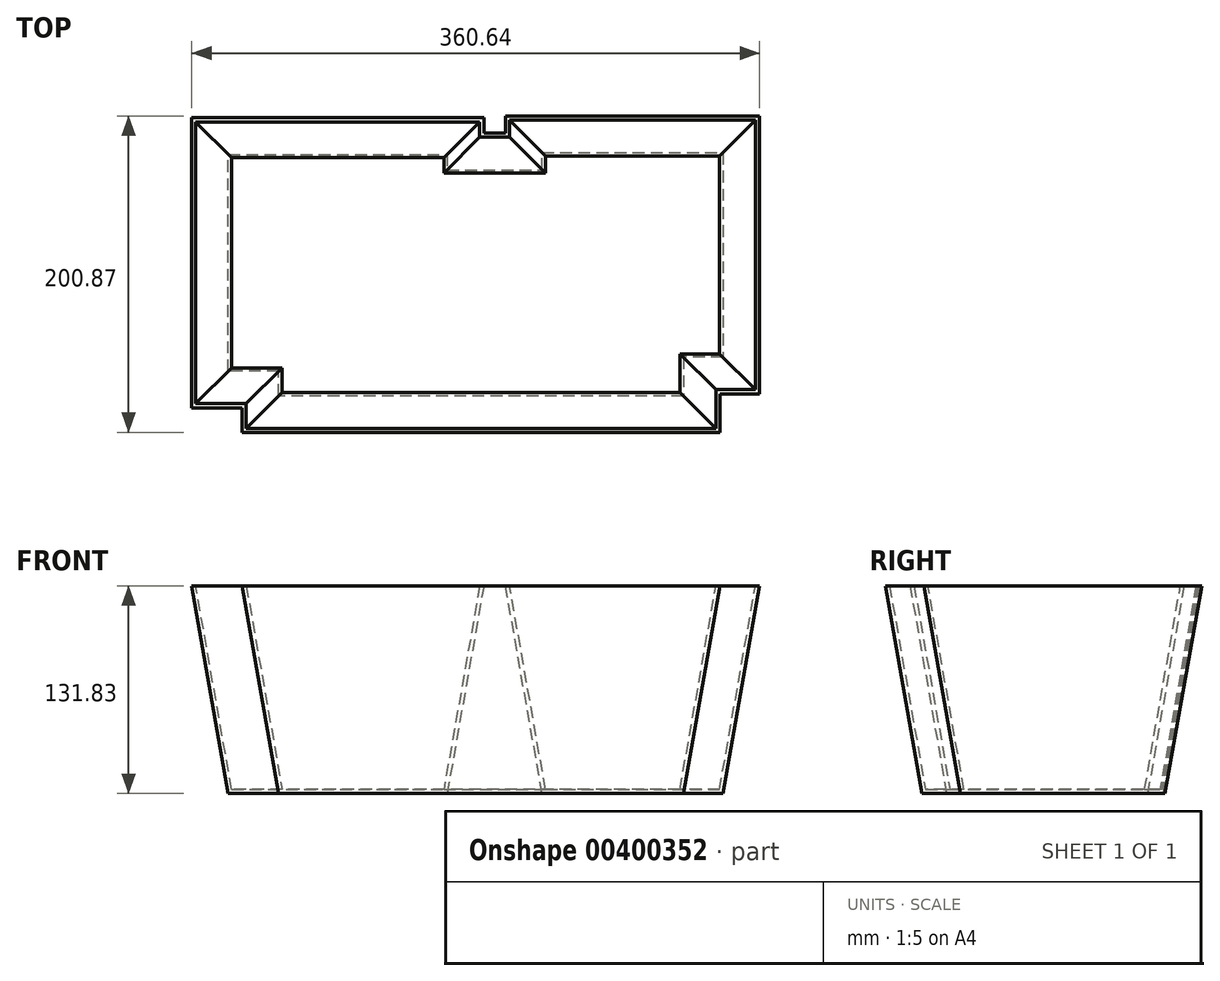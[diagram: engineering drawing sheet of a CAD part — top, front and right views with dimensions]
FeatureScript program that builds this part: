
annotation { "Feature Type Name" : "Feature", "Feature Type Description" : "" }
export const myFeature = defineFeature(function(context is Context, id is Id, definition is map)
    precondition{}
    {
        {
            var Q0;
            Q0=qCreatedBy(makeId("Top.planeOp"),FACE);
            var sketch = newSketch(context, id + "F0", { "sketchPlane" : qUnion([Q0])});
            skLineSegment(sketch, "E0.bottom", {"start": v(-39.3, 76.29) * mm, "end": v(21, 76.29) * mm});
            skLineSegment(sketch, "E0.top", {"start": v(-146.27, -67.2) * mm, "end": v(110.71, -67.2) * mm});
            skLineSegment(sketch, "E0.left", {"start": v(-146.27, -51.6) * mm, "end": v(-146.27, -67.2) * mm});
            skLineSegment(sketch, "E0.right", {"start": v(110.71, -42.72) * mm, "end": v(110.71, -67.2) * mm});
            skLineSegment(sketch, "E1.bottom", {"start": v(-178.34, 86.1) * mm, "end": v(-39.3, 86.1) * mm});
            skLineSegment(sketch, "E1.top", {"start": v(-178.34, -51.6) * mm, "end": v(-146.27, -51.6) * mm});
            skLineSegment(sketch, "E1.left", {"start": v(-178.34, 86.1) * mm, "end": v(-178.34, -51.6) * mm});
            skLineSegment(sketch, "E1.right", {"start": v(-39.3, 86.1) * mm, "end": v(-39.3, 76.29) * mm});
            skLineSegment(sketch, "E2.bottom", {"start": v(21, 87.18) * mm, "end": v(135.81, 87.18) * mm});
            skLineSegment(sketch, "E2.top", {"start": v(110.71, -42.72) * mm, "end": v(135.81, -42.72) * mm});
            skLineSegment(sketch, "E2.left", {"start": v(21, 87.18) * mm, "end": v(21, 76.29) * mm});
            skLineSegment(sketch, "E2.right", {"start": v(135.81, 87.18) * mm, "end": v(135.81, -42.72) * mm});
            skSolve(sketch);
        }
        {
            var Q0;
            Q0=makeQuery(id+"F0.imprint","IMPRINT",FACE,{"disambiguationData":[TD([[makeQuery(id+"F0.imprint","IMPRINT",EDGE,{"derivedFrom":sQuery(id+"F0.wireOp",EDGE,"E0.bottom")}),-1.0]])]});
            extrude(context, id + "F1", {"entities" : qUnion([Q0]), "depth" : 131.83 * mm, "hasDraft" : true, "draftAngle" : 10 * degree});
        }
        {
            var Q0;
            Q0=makeQuery(id+"F1.opExtrude","CAP_FACE",FACE,{"disambiguationData":[OSD([sQuery(id+"F0.wireOp",EDGE,"E0.bottom"),sQuery(id+"F0.wireOp",EDGE,"E0.top"),sQuery(id+"F0.wireOp",EDGE,"E0.left"),sQuery(id+"F0.wireOp",EDGE,"E0.right")])],"isStart":false});
            shell(context, id + "F2", {"entities" : qUnion([Q0]), "thickness" : 2.54 * mm});
        }
    });
